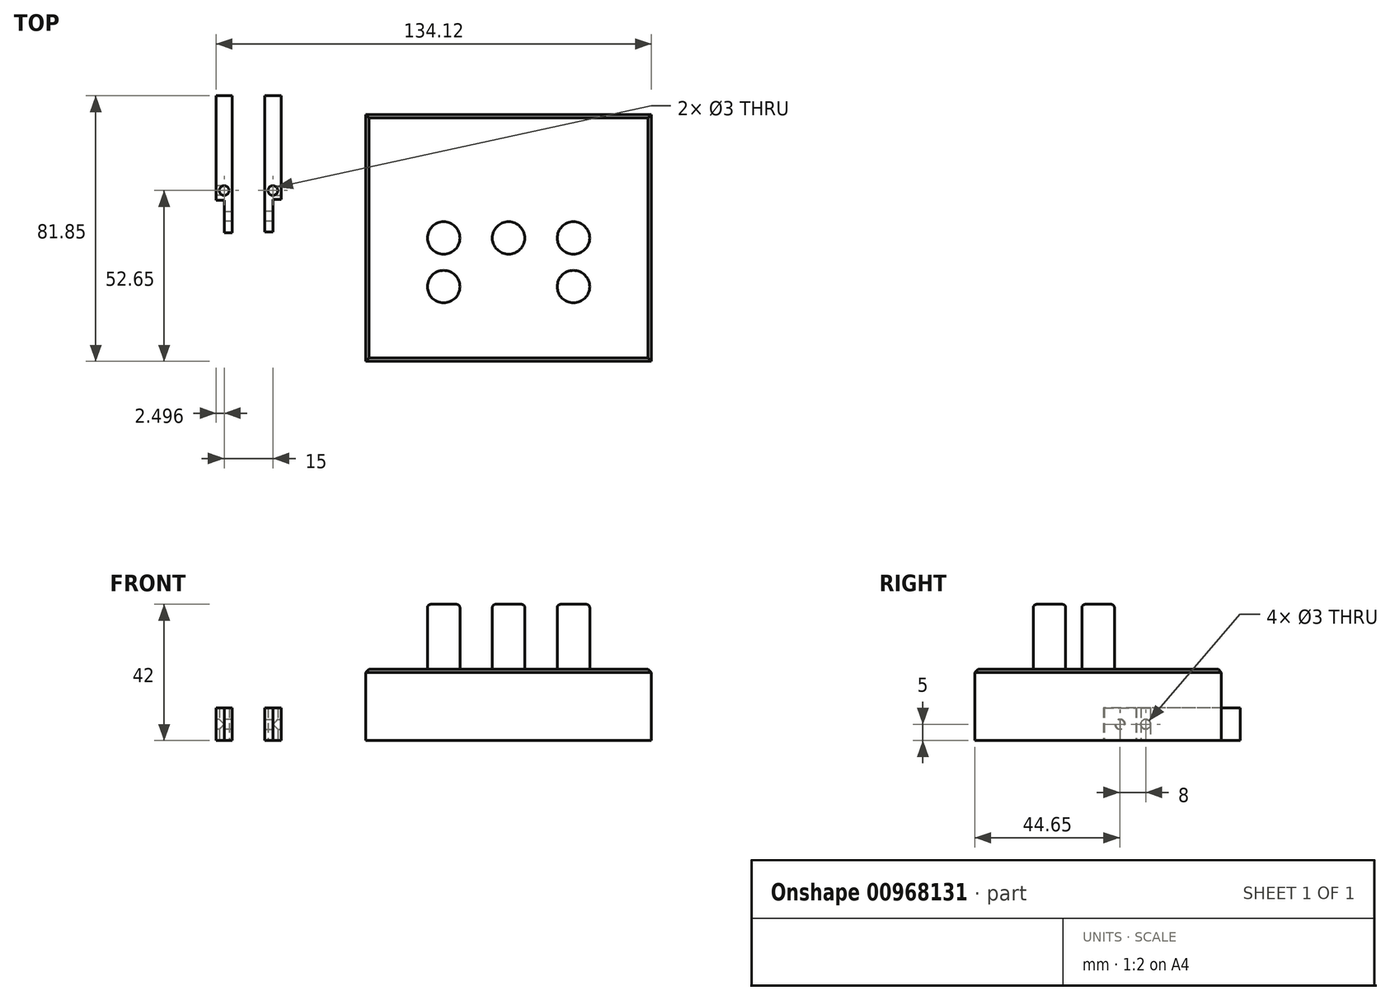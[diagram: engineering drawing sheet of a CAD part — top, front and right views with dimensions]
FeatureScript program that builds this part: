
annotation { "Feature Type Name" : "Feature", "Feature Type Description" : "" }
export const myFeature = defineFeature(function(context is Context, id is Id, definition is map)
    precondition{}
    {
        {
            var Q0;
            Q0=qCreatedBy(makeId("Top.planeOp"),FACE);
            var sketch = newSketch(context, id + "F0", { "sketchPlane" : qUnion([Q0])});
            skLineSegment(sketch, "E0.bottom", {"start": v(-34.11, 34.62) * mm, "end": v(53.89, 34.62) * mm});
            skLineSegment(sketch, "E0.top", {"start": v(-34.11, -41.38) * mm, "end": v(53.89, -41.38) * mm});
            skLineSegment(sketch, "E0.left", {"start": v(-34.11, 34.62) * mm, "end": v(-34.11, -41.38) * mm});
            skLineSegment(sketch, "E0.right", {"start": v(53.89, 34.62) * mm, "end": v(53.89, -41.38) * mm});
            skSolve(sketch);
        }
        {
            var Q0;
            Q0 = qSketchRegion(id + "F0", true);
            extrude(context, id + "F1", {"entities" : qUnion([Q0]), "depth" : 22 * mm, "offsetDistance" : 25 * mm});
        }
        {
            var Q0;
            Q0=makeQuery(id+"F1.opExtrude","CAP_EDGE",EDGE,{"disambiguationData":[OSD([sQuery(id+"F0.wireOp",EDGE,"E0.top")])],"isStart":false});
            var Q1;
            Q1=makeQuery(id+"F1.opExtrude","CAP_EDGE",EDGE,{"disambiguationData":[OSD([sQuery(id+"F0.wireOp",EDGE,"E0.left")])],"isStart":false});
            var Q2;
            Q2=makeQuery(id+"F1.opExtrude","CAP_EDGE",EDGE,{"disambiguationData":[OSD([sQuery(id+"F0.wireOp",EDGE,"E0.bottom")])],"isStart":false});
            var Q3;
            Q3=makeQuery(id+"F1.opExtrude","CAP_EDGE",EDGE,{"disambiguationData":[OSD([sQuery(id+"F0.wireOp",EDGE,"E0.right")])],"isStart":false});
            chamfer(context, id + "F2", {"entities" : qUnion([Q0, Q1, Q2, Q3]), "width" : 1 * mm, "tangentPropagation" : true});
        }
        {
            var Q0;
            Q0=makeQuery(id+"F1.opExtrude","CAP_FACE",FACE,{"disambiguationData":[OSD([sQuery(id+"F0.wireOp",EDGE,"E0.bottom"),sQuery(id+"F0.wireOp",EDGE,"E0.top"),sQuery(id+"F0.wireOp",EDGE,"E0.left"),sQuery(id+"F0.wireOp",EDGE,"E0.right")])],"isStart":false});
            var sketch = newSketch(context, id + "F3", { "sketchPlane" : qUnion([Q0])});
            skLineSegment(sketch, "E1", {"start": v(9.89, 33.62) * mm, "end": v(9.89, -40.38) * mm, "construction": true});
            skLineSegment(sketch, "E2", {"start": v(-33.11, -3.38) * mm, "end": v(52.89, -3.38) * mm, "construction": true});
            skCircle(sketch, "E3", {"center": v(9.89, -3.38) * mm, "radius": 5 * mm});
            skCircle(sketch, "E4", {"center": v(-10.11, -3.38) * mm, "radius": 5 * mm});
            skCircle(sketch, "E5", {"center": v(29.89, -3.38) * mm, "radius": 5 * mm});
            skCircle(sketch, "E6", {"center": v(-10.11, -18.38) * mm, "radius": 5 * mm});
            skCircle(sketch, "E7", {"center": v(29.89, -18.38) * mm, "radius": 5 * mm});
            skSolve(sketch);
        }
        {
            var Q0;
            Q0=makeQuery(id+"F3.imprint","IMPRINT",FACE,{"disambiguationData":[TD([[makeQuery(id+"F3.imprint","IMPRINT",EDGE,{"derivedFrom":sQuery(id+"F3.wireOp",EDGE,"E4")}),1.0]])]});
            var Q1;
            Q1=makeQuery(id+"F3.imprint","IMPRINT",FACE,{"disambiguationData":[TD([[makeQuery(id+"F3.imprint","IMPRINT",EDGE,{"derivedFrom":sQuery(id+"F3.wireOp",EDGE,"E3")}),1.0]])]});
            var Q2;
            Q2=makeQuery(id+"F3.imprint","IMPRINT",FACE,{"disambiguationData":[TD([[makeQuery(id+"F3.imprint","IMPRINT",EDGE,{"derivedFrom":sQuery(id+"F3.wireOp",EDGE,"E5")}),1.0]])]});
            var Q3;
            Q3=makeQuery(id+"F3.imprint","IMPRINT",FACE,{"disambiguationData":[TD([[makeQuery(id+"F3.imprint","IMPRINT",EDGE,{"derivedFrom":sQuery(id+"F3.wireOp",EDGE,"E7")}),1.0]])]});
            var Q4;
            Q4=makeQuery(id+"F3.imprint","IMPRINT",FACE,{"disambiguationData":[TD([[makeQuery(id+"F3.imprint","IMPRINT",EDGE,{"derivedFrom":sQuery(id+"F3.wireOp",EDGE,"E6")}),1.0]])]});
            var Q5;
            Q5=sQuery(id+"F3.wireOp",EDGE,"E4");
            var Q6;
            Q6=sQuery(id+"F3.wireOp",EDGE,"E3");
            var Q7;
            Q7=sQuery(id+"F3.wireOp",EDGE,"E5");
            var Q8;
            Q8=sQuery(id+"F3.wireOp",EDGE,"E7");
            var Q9;
            Q9=sQuery(id+"F3.wireOp",EDGE,"E6");
            extrude(context, id + "F4", {"entities" : qUnion([Q0, Q1, Q2, Q3, Q4]), "surfaceEntities" : qUnion([Q5, Q6, Q7, Q8, Q9]), "depth" : 20 * mm, "offsetDistance" : 25 * mm});
        }
        {
            var Q0;
            Q0=makeQuery(id+"F4.opExtrude","CAP_EDGE",EDGE,{"disambiguationData":[OSD([sQuery(id+"F3.wireOp",EDGE,"E4")])],"isStart":false});
            var Q1;
            Q1=makeQuery(id+"F4.opExtrude","CAP_EDGE",EDGE,{"disambiguationData":[OSD([sQuery(id+"F3.wireOp",EDGE,"E6")])],"isStart":false});
            var Q2;
            Q2=makeQuery(id+"F4.opExtrude","CAP_EDGE",EDGE,{"disambiguationData":[OSD([sQuery(id+"F3.wireOp",EDGE,"E3")])],"isStart":false});
            var Q3;
            Q3=makeQuery(id+"F4.opExtrude","CAP_EDGE",EDGE,{"disambiguationData":[OSD([sQuery(id+"F3.wireOp",EDGE,"E5")])],"isStart":false});
            var Q4;
            Q4=makeQuery(id+"F4.opExtrude","CAP_EDGE",EDGE,{"disambiguationData":[OSD([sQuery(id+"F3.wireOp",EDGE,"E7")])],"isStart":false});
            fillet(context, id + "F5", {"entities" : qUnion([Q0, Q1, Q2, Q3, Q4]), "radius" : 1 * mm, "tangentPropagation" : true, "allowEdgeOverflow" : false});
        }
        {
            var Q0;
            Q0=qCreatedBy(makeId("Top.planeOp"),FACE);
            var sketch = newSketch(context, id + "F6", { "sketchPlane" : qUnion([Q0])});
            skLineSegment(sketch, "E8.bottom", {"start": v(-80.23, 40.47) * mm, "end": v(-75.23, 40.47) * mm});
            skLineSegment(sketch, "E8.left", {"start": v(-80.23, 40.47) * mm, "end": v(-80.23, -1.53) * mm});
            skLineSegment(sketch, "E8.right", {"start": v(-75.23, 40.47) * mm, "end": v(-75.23, -1.73) * mm});
            skLineSegment(sketch, "E9.bottom", {"start": v(-65.23, 40.47) * mm, "end": v(-60.23, 40.47) * mm});
            skLineSegment(sketch, "E9.top", {"start": v(-65.23, -1.53) * mm, "end": v(-60.23, -1.53) * mm});
            skLineSegment(sketch, "E9.left", {"start": v(-65.23, 40.47) * mm, "end": v(-65.23, -1.53) * mm});
            skLineSegment(sketch, "E9.right", {"start": v(-60.23, 40.47) * mm, "end": v(-60.23, -1.53) * mm});
            skCircle(sketch, "E10", {"center": v(-77.73, 11.27) * mm, "radius": 1.5 * mm});
            skCircle(sketch, "E11", {"center": v(-62.73, 11.27) * mm, "radius": 1.5 * mm});
            skLineSegment(sketch, "E12.bottom", {"start": v(-77.73, -1.73) * mm, "end": v(-75.23, -1.73) * mm});
            skLineSegment(sketch, "E13.bottom", {"start": v(-77.73, -1.73) * mm, "end": v(-80.23, -1.73) * mm});
            skLineSegment(sketch, "E13.top", {"start": v(-77.73, 8.27) * mm, "end": v(-80.23, 8.27) * mm});
            skLineSegment(sketch, "E13.left", {"start": v(-77.73, -1.73) * mm, "end": v(-77.73, 8.27) * mm});
            skLineSegment(sketch, "E13.right", {"start": v(-80.23, -1.73) * mm, "end": v(-80.23, 8.27) * mm});
            skLineSegment(sketch, "E14.bottom", {"start": v(-62.73, -1.53) * mm, "end": v(-60.23, -1.53) * mm});
            skLineSegment(sketch, "E14.top", {"start": v(-62.73, 8.47) * mm, "end": v(-60.23, 8.47) * mm});
            skLineSegment(sketch, "E14.left", {"start": v(-62.73, -1.53) * mm, "end": v(-62.73, 8.47) * mm});
            skLineSegment(sketch, "E14.right", {"start": v(-60.23, -1.53) * mm, "end": v(-60.23, 8.47) * mm});
            skSolve(sketch);
        }
        {
            var Q0;
            Q0=makeQuery(id+"F6.imprint","IMPRINT",FACE,{"disambiguationData":[TD([[makeQuery(id+"F6.imprint","IMPRINT",EDGE,{"derivedFrom":sQuery(id+"F6.wireOp",EDGE,"E9.bottom")}),-1.0]])]});
            var Q1;
            Q1=makeQuery(id+"F6.imprint","IMPRINT",FACE,{"disambiguationData":[TD([[makeQuery(id+"F6.imprint","IMPRINT",EDGE,{"derivedFrom":sQuery(id+"F6.wireOp",EDGE,"E8.bottom")}),-1.0]])]});
            extrude(context, id + "F7", {"entities" : qUnion([Q0, Q1]), "depth" : 10 * mm, "offsetDistance" : 25 * mm});
        }
        {
            var Q0;
            Q0=makeQuery(id+"F7.opExtrude","SWEPT_FACE",FACE,{"disambiguationData":[OSD([sQuery(id+"F6.wireOp",EDGE,"E8.left")])]});
            var sketch = newSketch(context, id + "F8", { "sketchPlane" : qUnion([Q0])});
            skLineSegment(sketch, "E15", {"start": v(-8.27, 5) * mm, "end": v(-40.47, 5) * mm, "construction": true});
            skLineSegment(sketch, "E16", {"start": v(-11.27, 10) * mm, "end": v(-11.27, 0) * mm, "construction": true});
            skCircle(sketch, "E17", {"center": v(-11.27, 5) * mm, "radius": 1.5 * mm});
            skSolve(sketch);
        }
        {
            var Q0;
            Q0=makeQuery(id+"F8.imprint","IMPRINT",FACE,{"disambiguationData":[TD([[makeQuery(id+"F8.imprint","IMPRINT",EDGE,{"derivedFrom":sQuery(id+"F8.wireOp",EDGE,"E17")}),1.0]])]});
            extrude(context, id + "F9", {"entities" : qUnion([Q0]), "operationType" : NewBodyOperationType.REMOVE, "oppositeDirection" : true, "depth" : 2.5 * mm, "offsetDistance" : 25 * mm});
        }
        {
            var Q0;
            Q0=makeQuery(id+"F7.opExtrude","SWEPT_FACE",FACE,{"disambiguationData":[OSD([sQuery(id+"F6.wireOp",EDGE,"E13.left")])]});
            var sketch = newSketch(context, id + "F10", { "sketchPlane" : qUnion([Q0])});
            skLineSegment(sketch, "E18", {"start": v(1.73, 5) * mm, "end": v(-8.27, 5) * mm, "construction": true});
            skCircle(sketch, "E19", {"center": v(-3.27, 5) * mm, "radius": 1.5 * mm});
            skSolve(sketch);
        }
        {
            var Q0;
            Q0=makeQuery(id+"F10.imprint","IMPRINT",FACE,{"disambiguationData":[TD([[makeQuery(id+"F10.imprint","IMPRINT",EDGE,{"derivedFrom":sQuery(id+"F10.wireOp",EDGE,"E19")}),1.0]])]});
            var Q1;
            Q1=sQuery(id+"F10.wireOp",EDGE,"E19");
            extrude(context, id + "F11", {"entities" : qUnion([Q0]), "operationType" : NewBodyOperationType.REMOVE, "surfaceEntities" : qUnion([Q1]), "oppositeDirection" : true, "depth" : 2.5 * mm, "offsetDistance" : 25 * mm});
        }
        {
            var Q0;
            Q0=makeQuery(id+"F7.opExtrude","SWEPT_FACE",FACE,{"disambiguationData":[OSD([sQuery(id+"F6.wireOp",EDGE,"E9.right")])]});
            var sketch = newSketch(context, id + "F12", { "sketchPlane" : qUnion([Q0])});
            skLineSegment(sketch, "E20", {"start": v(11.27, 10) * mm, "end": v(11.27, 0) * mm, "construction": true});
            skCircle(sketch, "E21", {"center": v(11.27, 5) * mm, "radius": 1.5 * mm});
            skSolve(sketch);
        }
        {
            var Q0;
            Q0=makeQuery(id+"F12.imprint","IMPRINT",FACE,{"disambiguationData":[TD([[makeQuery(id+"F12.imprint","IMPRINT",EDGE,{"derivedFrom":sQuery(id+"F12.wireOp",EDGE,"E21")}),1.0]])]});
            var Q1;
            Q1=sQuery(id+"F12.wireOp",EDGE,"E21");
            extrude(context, id + "F13", {"entities" : qUnion([Q0]), "operationType" : NewBodyOperationType.REMOVE, "surfaceEntities" : qUnion([Q1]), "oppositeDirection" : true, "depth" : 2.5 * mm, "offsetDistance" : 25 * mm});
        }
        {
            var Q0;
            Q0=makeQuery(id+"F7.opExtrude","SWEPT_FACE",FACE,{"disambiguationData":[OSD([sQuery(id+"F6.wireOp",EDGE,"E14.left")])]});
            var sketch = newSketch(context, id + "F14", { "sketchPlane" : qUnion([Q0])});
            skLineSegment(sketch, "E22", {"start": v(-1.53, 5) * mm, "end": v(8.47, 5) * mm, "construction": true});
            skCircle(sketch, "E23", {"center": v(3.47, 5) * mm, "radius": 1.5 * mm});
            skSolve(sketch);
        }
        {
            var Q0;
            Q0=makeQuery(id+"F14.imprint","IMPRINT",FACE,{"disambiguationData":[TD([[makeQuery(id+"F14.imprint","IMPRINT",EDGE,{"derivedFrom":sQuery(id+"F14.wireOp",EDGE,"E23")}),1.0]])]});
            var Q1;
            Q1=sQuery(id+"F14.wireOp",EDGE,"E23");
            extrude(context, id + "F15", {"entities" : qUnion([Q0]), "operationType" : NewBodyOperationType.REMOVE, "surfaceEntities" : qUnion([Q1]), "oppositeDirection" : true, "depth" : 2.5 * mm, "offsetDistance" : 25 * mm});
        }
    });
